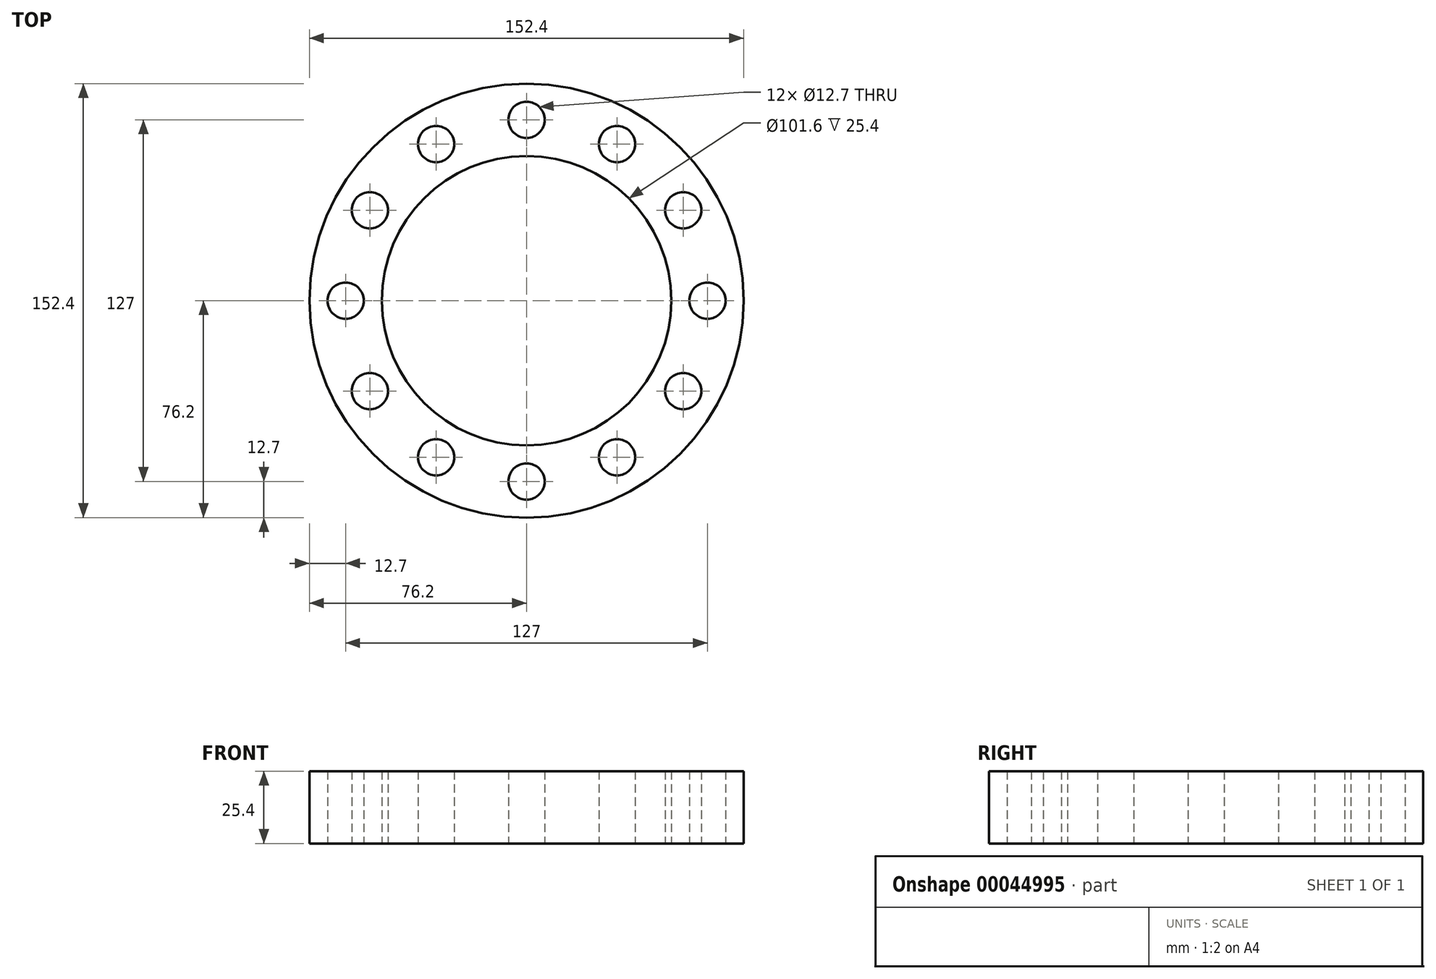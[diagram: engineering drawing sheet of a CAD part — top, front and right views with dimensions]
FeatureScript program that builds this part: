
annotation { "Feature Type Name" : "Feature", "Feature Type Description" : "" }
export const myFeature = defineFeature(function(context is Context, id is Id, definition is map)
    precondition{}
    {
        {
            var Q0;
            Q0=qCreatedBy(makeId("Top.planeOp"),FACE);
            var sketch = newSketch(context, id + "F0", { "sketchPlane" : qUnion([Q0])});
            skCircle(sketch, "E0", {"center": v(0, 0) * mm, "radius": 76.2 * mm});
            skCircle(sketch, "E1", {"center": v(0, 0) * mm, "radius": 50.8 * mm});
            skCircle(sketch, "E2", {"center": v(0, 63.5) * mm, "radius": 6.35 * mm});
            skCircle(sketch, "E3.1.0", {"center": v(31.75, 55) * mm, "radius": 6.35 * mm});
            skCircle(sketch, "E3.2.0", {"center": v(55, 31.75) * mm, "radius": 6.35 * mm});
            skCircle(sketch, "E3.3.0", {"center": v(63.5, 0) * mm, "radius": 6.35 * mm});
            skCircle(sketch, "E3.4.0", {"center": v(55, -31.75) * mm, "radius": 6.35 * mm});
            skCircle(sketch, "E3.5.0", {"center": v(31.75, -55) * mm, "radius": 6.35 * mm});
            skCircle(sketch, "E3.6.0", {"center": v(0, -63.5) * mm, "radius": 6.35 * mm});
            skCircle(sketch, "E3.7.0", {"center": v(-31.75, -55) * mm, "radius": 6.35 * mm});
            skCircle(sketch, "E3.8.0", {"center": v(-55, -31.75) * mm, "radius": 6.35 * mm});
            skCircle(sketch, "E3.9.0", {"center": v(-63.5, 0) * mm, "radius": 6.35 * mm});
            skCircle(sketch, "E3.10.0", {"center": v(-55, 31.75) * mm, "radius": 6.35 * mm});
            skCircle(sketch, "E3.11.0", {"center": v(-31.75, 55) * mm, "radius": 6.35 * mm});
            skLineSegment(sketch, "E3.anchor1", {"start": v(0, 0) * mm, "end": v(0, 63.5) * mm, "construction": true});
            skLineSegment(sketch, "E3.anchor2", {"start": v(0, 0) * mm, "end": v(-31.75, 55) * mm, "construction": true});
            skSolve(sketch);
        }
        {
            var Q0;
            Q0=makeQuery(id+"F0.imprint","IMPRINT",FACE,{"disambiguationData":[TD([[makeQuery(id+"F0.imprint","IMPRINT",EDGE,{"derivedFrom":sQuery(id+"F0.wireOp",EDGE,"E0")}),1.0]])]});
            extrude(context, id + "F1", {"entities" : qUnion([Q0]), "depth" : 25.4 * mm});
        }
    });
